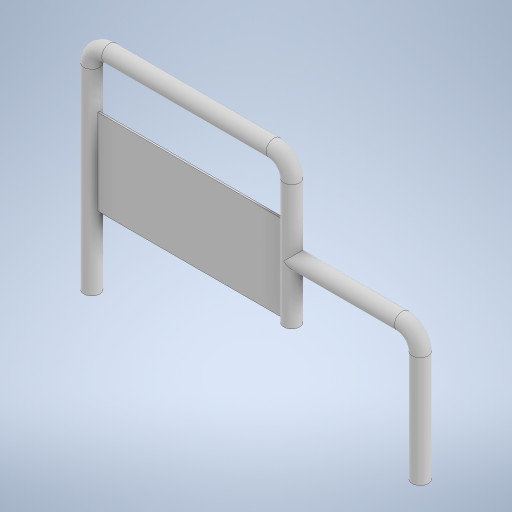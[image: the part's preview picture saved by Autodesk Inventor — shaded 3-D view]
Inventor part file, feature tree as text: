
AUTODESK INVENTOR PART (.ipt)
format: ipt  version: 2023 (Build 270158000, 158)  size: 280,064 bytes
history: native  units: in
note: dims shown in document units (in); Inventor stores cm internally (conversion verified against a paired STEP export)
features: sketch x6, sweep x2, plane x1, extrude x1
ambient origin geometry x8: Origin, YZ Plane, XZ Plane, XY Plane, X Axis, Y Axis, Z Axis, Center Point
bodies: Solid1 (feature_tree)
feature tree (10):
  sweep  "Sweep1"
  sketch  "Sketch3"  dims[d4=0.9843in d5=0.9843in]
  sketch  "Sketch4"  dims[d6=0.9843in]
  plane  "Work Plane1"
  sweep  "Sweep2"
  extrude  "Extrusion1"  Depth=0.9843in
  sketch  "Sketch1"  dims[d0=11.811in d1=11.0236in]
  sketch  "Sketch2"  dims[d2=4.7244in d3=7.0866in]
  sketch  "Sketch5"  dims[d7=3.4148in]
  sketch  "Sketch6"  dims[d8=0.8858in d9=0.0in d10=0.0in d11=3.1496in d12=3.937in d13=0.8858in d14=0.0in d15=0.0in d16=4.7244in d17=0.0984in d18=0.0in]
